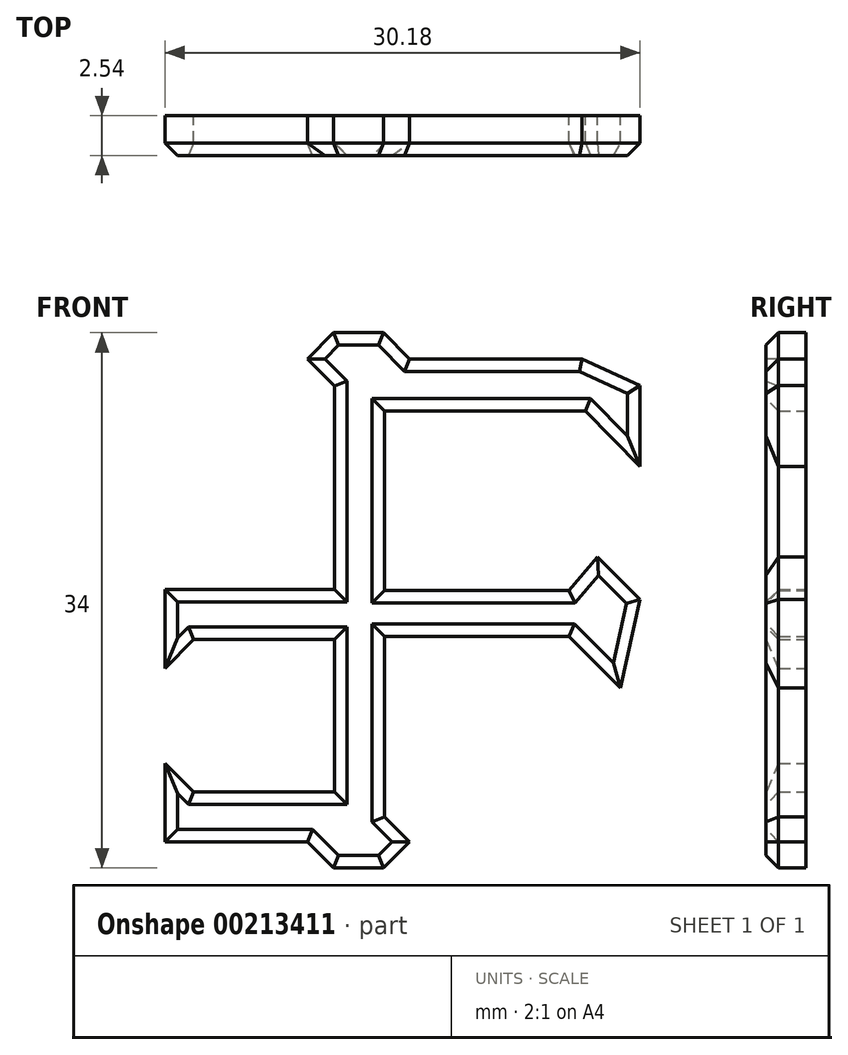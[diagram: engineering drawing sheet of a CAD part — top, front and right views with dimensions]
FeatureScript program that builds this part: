
annotation { "Feature Type Name" : "Feature", "Feature Type Description" : "" }
export const myFeature = defineFeature(function(context is Context, id is Id, definition is map)
    precondition{}
    {
        {
            var Q0;
            Q0=qCreatedBy(makeId("Front.planeOp"),FACE);
            var sketch = newSketch(context, id + "F0", { "sketchPlane" : qUnion([Q0])});
            skLineSegment(sketch, "E0", {"start": v(-3.18, 25.96) * mm, "end": v(-6.65, 29.43) * mm});
            skLineSegment(sketch, "E1", {"start": v(6.35, 29.43) * mm, "end": v(28.26, 29.43) * mm});
            skLineSegment(sketch, "E2", {"start": v(28.26, 29.43) * mm, "end": v(35.62, 26.07) * mm});
            skLineSegment(sketch, "E3", {"start": v(35.62, 15.75) * mm, "end": v(28.66, 22.79) * mm});
            skLineSegment(sketch, "E4", {"start": v(28.66, 22.79) * mm, "end": v(3.17, 22.79) * mm});
            skLineSegment(sketch, "E5", {"start": v(3.17, 22.79) * mm, "end": v(3.18, 0) * mm});
            skLineSegment(sketch, "E6", {"start": v(3.18, 0) * mm, "end": v(26.6, 0) * mm});
            skLineSegment(sketch, "E7", {"start": v(26.6, 0) * mm, "end": v(30.23, 4.24) * mm});
            skLineSegment(sketch, "E8", {"start": v(30.23, 4.24) * mm, "end": v(35.62, -1.15) * mm});
            skLineSegment(sketch, "E9", {"start": v(35.62, -1.15) * mm, "end": v(33.14, -12.36) * mm});
            skLineSegment(sketch, "E10", {"start": v(33.14, -12.36) * mm, "end": v(26.6, -5.82) * mm});
            skLineSegment(sketch, "E11", {"start": v(26.6, -5.82) * mm, "end": v(3.18, -5.82) * mm});
            skLineSegment(sketch, "E12", {"start": v(3.18, -5.82) * mm, "end": v(3.18, -28.75) * mm});
            skLineSegment(sketch, "E13", {"start": v(3.18, -28.75) * mm, "end": v(6.35, -31.93) * mm});
            skLineSegment(sketch, "E14", {"start": v(-6.65, 29.43) * mm, "end": v(-3.32, 32.76) * mm});
            skPoint(sketch, "E14.endSnap0", {"position": v(-3.32, 26.11) * mm});
            skLineSegment(sketch, "E15", {"start": v(-3.32, 32.76) * mm, "end": v(3.03, 32.76) * mm});
            skLineSegment(sketch, "E16", {"start": v(3.03, 32.76) * mm, "end": v(6.35, 29.43) * mm});
            skPoint(sketch, "E17.startSnap0", {"position": v(2.15, -36.37) * mm});
            skLineSegment(sketch, "E18", {"start": v(-6.65, -31.93) * mm, "end": v(-22.13, -31.93) * mm});
            skLineSegment(sketch, "E19", {"start": v(-22.13, -31.93) * mm, "end": v(-24.74, -31.93) * mm});
            skLineSegment(sketch, "E20", {"start": v(-24.74, -31.93) * mm, "end": v(-24.74, -21.93) * mm});
            skLineSegment(sketch, "E21", {"start": v(-24.74, -21.93) * mm, "end": v(-21.1, -25.58) * mm});
            skLineSegment(sketch, "E22", {"start": v(-21.1, -25.58) * mm, "end": v(-3.17, -25.58) * mm});
            skLineSegment(sketch, "E23", {"start": v(-3.17, -25.58) * mm, "end": v(-3.18, -6.24) * mm});
            skLineSegment(sketch, "E24", {"start": v(-3.18, -6.24) * mm, "end": v(-21.1, -6.24) * mm});
            skLineSegment(sketch, "E25", {"start": v(-21.1, -6.24) * mm, "end": v(-24.74, -9.88) * mm});
            skLineSegment(sketch, "E26", {"start": v(-24.74, -9.88) * mm, "end": v(-24.74, 0.11) * mm});
            skLineSegment(sketch, "E27", {"start": v(-24.74, 0.11) * mm, "end": v(-3.17, 0.11) * mm});
            skLineSegment(sketch, "E28", {"start": v(0, 22.79) * mm, "end": v(0, 0.11) * mm});
            skLineSegment(sketch, "E29", {"start": v(-3.18, 25.96) * mm, "end": v(-3.17, 0.11) * mm});
            skLineSegment(sketch, "E30", {"start": v(-6.65, -31.93) * mm, "end": v(-3.32, -35.25) * mm});
            skLineSegment(sketch, "E31", {"start": v(-3.32, -35.25) * mm, "end": v(3.03, -35.25) * mm});
            skLineSegment(sketch, "E32", {"start": v(3.03, -35.25) * mm, "end": v(6.35, -31.93) * mm});
            skPoint(sketch, "E33.orphan", {"position": v(-3.17, -31.93) * mm});
            skLineSegment(sketch, "E34", {"start": v(35.62, 26.07) * mm, "end": v(35.62, 15.75) * mm});
            skSolve(sketch);
        }
        {
            var Q0;
            Q0=makeQuery(id+"F0.imprint","IMPRINT",FACE,{"disambiguationData":[TD([[makeQuery(id+"F0.imprint","IMPRINT",EDGE,{"derivedFrom":sQuery(id+"F0.wireOp",EDGE,"E0")}),-1.0]])]});
            extrude(context, id + "F1", {"entities" : qUnion([Q0]), "depth" : 5.08 * mm});
        }
        {
            var Q0;
            Q0=makeQuery(id+"F1.opExtrude","CAP_FACE",FACE,{"disambiguationData":[OSD([sQuery(id+"F0.wireOp",EDGE,"E0"),sQuery(id+"F0.wireOp",EDGE,"E1"),sQuery(id+"F0.wireOp",EDGE,"E2"),sQuery(id+"F0.wireOp",EDGE,"E3"),sQuery(id+"F0.wireOp",EDGE,"E4"),sQuery(id+"F0.wireOp",EDGE,"E5"),sQuery(id+"F0.wireOp",EDGE,"E6"),sQuery(id+"F0.wireOp",EDGE,"E7"),sQuery(id+"F0.wireOp",EDGE,"E8"),sQuery(id+"F0.wireOp",EDGE,"E9"),sQuery(id+"F0.wireOp",EDGE,"E10"),sQuery(id+"F0.wireOp",EDGE,"E11"),sQuery(id+"F0.wireOp",EDGE,"E12"),sQuery(id+"F0.wireOp",EDGE,"E13"),sQuery(id+"F0.wireOp",EDGE,"E14"),sQuery(id+"F0.wireOp",EDGE,"E15"),sQuery(id+"F0.wireOp",EDGE,"E16"),sQuery(id+"F0.wireOp",EDGE,"E18"),sQuery(id+"F0.wireOp",EDGE,"E19"),sQuery(id+"F0.wireOp",EDGE,"E20"),sQuery(id+"F0.wireOp",EDGE,"E21"),sQuery(id+"F0.wireOp",EDGE,"E22"),sQuery(id+"F0.wireOp",EDGE,"E23"),sQuery(id+"F0.wireOp",EDGE,"E24"),sQuery(id+"F0.wireOp",EDGE,"E25"),sQuery(id+"F0.wireOp",EDGE,"E26"),sQuery(id+"F0.wireOp",EDGE,"E27"),sQuery(id+"F0.wireOp",EDGE,"E29"),sQuery(id+"F0.wireOp",EDGE,"E30"),sQuery(id+"F0.wireOp",EDGE,"E31"),sQuery(id+"F0.wireOp",EDGE,"E32"),sQuery(id+"F0.wireOp",EDGE,"E34")])],"isStart":false});
            chamfer(context, id + "F2", {"entities" : qUnion([Q0]), "width" : 1.59 * mm, "tangentPropagation" : true});
        }
        {
            var Q0;
            Q0=makeQuery(id+"F1.opExtrude","SWEPT_BODY",BODY,{"disambiguationData":[OSD([sQuery(id+"F0.wireOp",EDGE,"E0"),sQuery(id+"F0.wireOp",EDGE,"E1"),sQuery(id+"F0.wireOp",EDGE,"E2"),sQuery(id+"F0.wireOp",EDGE,"E3"),sQuery(id+"F0.wireOp",EDGE,"E4"),sQuery(id+"F0.wireOp",EDGE,"E5"),sQuery(id+"F0.wireOp",EDGE,"E6"),sQuery(id+"F0.wireOp",EDGE,"E7"),sQuery(id+"F0.wireOp",EDGE,"E8"),sQuery(id+"F0.wireOp",EDGE,"E9"),sQuery(id+"F0.wireOp",EDGE,"E10"),sQuery(id+"F0.wireOp",EDGE,"E11"),sQuery(id+"F0.wireOp",EDGE,"E12"),sQuery(id+"F0.wireOp",EDGE,"E13"),sQuery(id+"F0.wireOp",EDGE,"E14"),sQuery(id+"F0.wireOp",EDGE,"E15"),sQuery(id+"F0.wireOp",EDGE,"E16"),sQuery(id+"F0.wireOp",EDGE,"E18"),sQuery(id+"F0.wireOp",EDGE,"E19"),sQuery(id+"F0.wireOp",EDGE,"E20"),sQuery(id+"F0.wireOp",EDGE,"E21"),sQuery(id+"F0.wireOp",EDGE,"E22"),sQuery(id+"F0.wireOp",EDGE,"E23"),sQuery(id+"F0.wireOp",EDGE,"E24"),sQuery(id+"F0.wireOp",EDGE,"E25"),sQuery(id+"F0.wireOp",EDGE,"E26"),sQuery(id+"F0.wireOp",EDGE,"E27"),sQuery(id+"F0.wireOp",EDGE,"E29"),sQuery(id+"F0.wireOp",EDGE,"E30"),sQuery(id+"F0.wireOp",EDGE,"E31"),sQuery(id+"F0.wireOp",EDGE,"E32"),sQuery(id+"F0.wireOp",EDGE,"E34")])]});
            var Q1;
            Q1=qCreatedBy(makeId("Origin.pointOp"),VERTEX);
            transform(context, id + "F3", {"entities" : qUnion([Q0]), "transformType" : TransformType.SCALE_UNIFORMLY, "scale" : .5, "scalePoint" : qUnion([Q1]), "makeCopy" : false});
        }
    });
